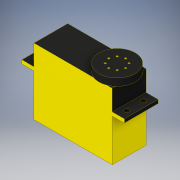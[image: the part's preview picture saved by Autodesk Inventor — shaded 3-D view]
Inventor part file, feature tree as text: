
AUTODESK INVENTOR PART (.ipt)
format: ipt  version: 2019 (Build 230136000, 136)  size: 199,168 bytes
history: native  units: mm
features: extrude x5, sketch x4
ambient origin geometry x8: Origin, YZ Plane, XZ Plane, XY Plane, X Axis, Y Axis, Z Axis, Center Point
bodies: Solid1 (feature_tree)
feature tree (9):
  extrude  "Extrusion1"  Depth=28.0mm
  extrude  "Extrusion2"  Depth=10.0mm
  extrude  "Extrusion3"  Depth=6.0mm TaperAngle=0.0deg
  extrude  "Extrusion4"  Depth=17.0mm
  extrude  "Extrusion5"  Depth=17.0mm TaperAngle=360.0deg
  sketch  "Sketch2"  dims[d0=65.0mm d1=28.0mm]
  sketch  "Sketch3"  dims[d2=55.0mm d3=0.0mm d4=10.0mm]
  sketch  "Sketch4"  dims[d5=30.0mm d6=6.0mm d7=0.0mm]
  sketch  "Sketch5"  dims[d12=1.6mm d14=7.0mm d15=80.0mm d17=360.0deg d19=3.5mm d20=0.0mm d21=4.0mm d22=14.0mm d23=7.0mm d26=20.0mm d27=0.0mm d28=14.0mm d29=5.0mm d30=5.0mm d31=5.0mm d32=5.0mm d33=17.0mm d34=0.0mm]
